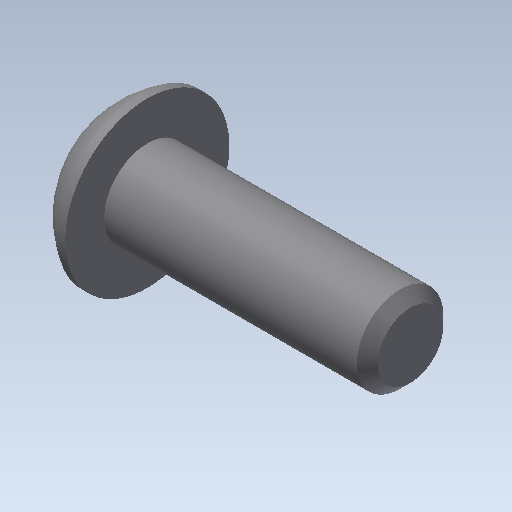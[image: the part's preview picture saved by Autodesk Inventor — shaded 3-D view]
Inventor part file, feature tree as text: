
AUTODESK INVENTOR PART (.ipt)
format: ipt  version: 2020 (Build 240168000, 168)  size: 143,360 bytes
history: native  units: in
note: dims shown in document units (in); Inventor stores cm internally (conversion verified against a paired STEP export)
features: other x3, extrude x1, chamfer x1, imported_body x1, sketch x1
ambient origin geometry x8: Origin, YZ Plane, XZ Plane, XY Plane, X Axis, Y Axis, Z Axis, Center Point
bodies: Body1 (feature_tree)
feature tree (7):
  other  "Bolt 0.5 inch"
  parser-record x1  (decoder bookkeeping rows leaked as tree rows — omitted from the tree; the rows remain in map.json)
  other  "Bolt"
  extrude  "thread length"  Depth=0.5in TaperAngle=0.0deg
  chamfer  "thread chamfer"  Distance=0.02in Angle=45.0deg
  imported_body  "Base1"
  sketch  "Sketch1"  dims[d0=0.164in d1=0.5in d2=0.0in d3=0.02in d4=0.125in d5=45.0deg d7=0.0in d9=0.0in]
